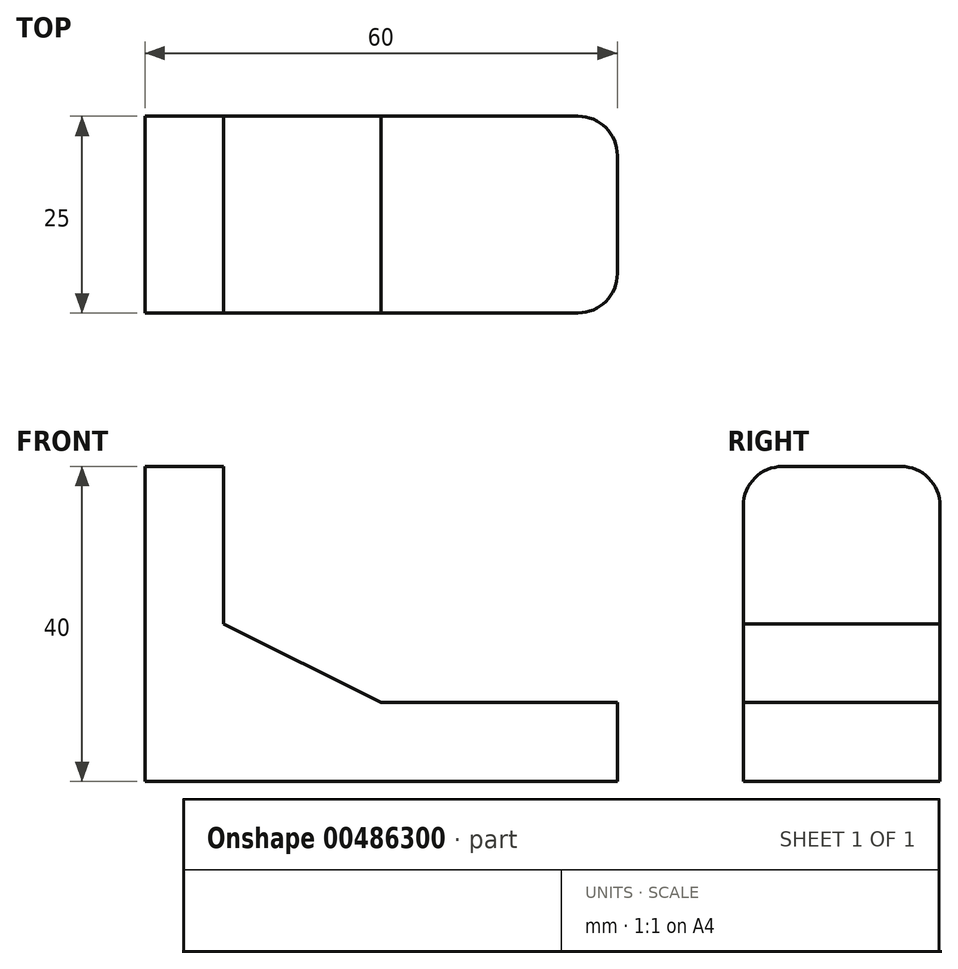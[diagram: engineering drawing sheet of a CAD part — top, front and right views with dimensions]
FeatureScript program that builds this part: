
annotation { "Feature Type Name" : "Feature", "Feature Type Description" : "" }
export const myFeature = defineFeature(function(context is Context, id is Id, definition is map)
    precondition{}
    {
        {
            var Q0;
            Q0=qCreatedBy(makeId("Front.planeOp"),FACE);
            var sketch = newSketch(context, id + "F0", { "sketchPlane" : qUnion([Q0])});
            skLineSegment(sketch, "E0", {"start": v(0, 0) * mm, "end": v(0, 40) * mm});
            skLineSegment(sketch, "E1", {"start": v(0, 40) * mm, "end": v(10, 40) * mm});
            skLineSegment(sketch, "E2", {"start": v(0, 0) * mm, "end": v(60, 0) * mm});
            skLineSegment(sketch, "E3", {"start": v(60, 0) * mm, "end": v(60, 10) * mm});
            skLineSegment(sketch, "E4", {"start": v(60, 10) * mm, "end": v(30, 10) * mm});
            skLineSegment(sketch, "E5", {"start": v(10, 40) * mm, "end": v(10, 20) * mm});
            skLineSegment(sketch, "E6", {"start": v(10, 20) * mm, "end": v(30, 10) * mm});
            skSolve(sketch);
        }
        {
            var Q0;
            Q0=makeQuery(id+"F0.imprint","IMPRINT",FACE,{"disambiguationData":[TD([[makeQuery(id+"F0.imprint","IMPRINT",EDGE,{"derivedFrom":sQuery(id+"F0.wireOp",EDGE,"E0")}),-1.0]])]});
            extrude(context, id + "F1", {"entities" : qUnion([Q0]), "depth" : 25 * mm});
        }
        {
            var Q0;
            Q0=makeQuery(id+"F1.opExtrude","CAP_EDGE",EDGE,{"disambiguationData":[OSD([sQuery(id+"F0.wireOp",EDGE,"E1")])],"isStart":false});
            var Q1;
            Q1=makeQuery(id+"F1.opExtrude","CAP_EDGE",EDGE,{"disambiguationData":[OSD([sQuery(id+"F0.wireOp",EDGE,"E1")])],"isStart":true});
            var Q2;
            Q2=makeQuery(id+"F1.opExtrude","CAP_EDGE",EDGE,{"disambiguationData":[OSD([sQuery(id+"F0.wireOp",EDGE,"E3")])],"isStart":false});
            var Q3;
            Q3=makeQuery(id+"F1.opExtrude","CAP_EDGE",EDGE,{"disambiguationData":[OSD([sQuery(id+"F0.wireOp",EDGE,"E3")])],"isStart":true});
            fillet(context, id + "F2", {"entities" : qUnion([Q0, Q1, Q2, Q3]), "radius" : 5 * mm, "tangentPropagation" : true, "allowEdgeOverflow" : false});
        }
    });
